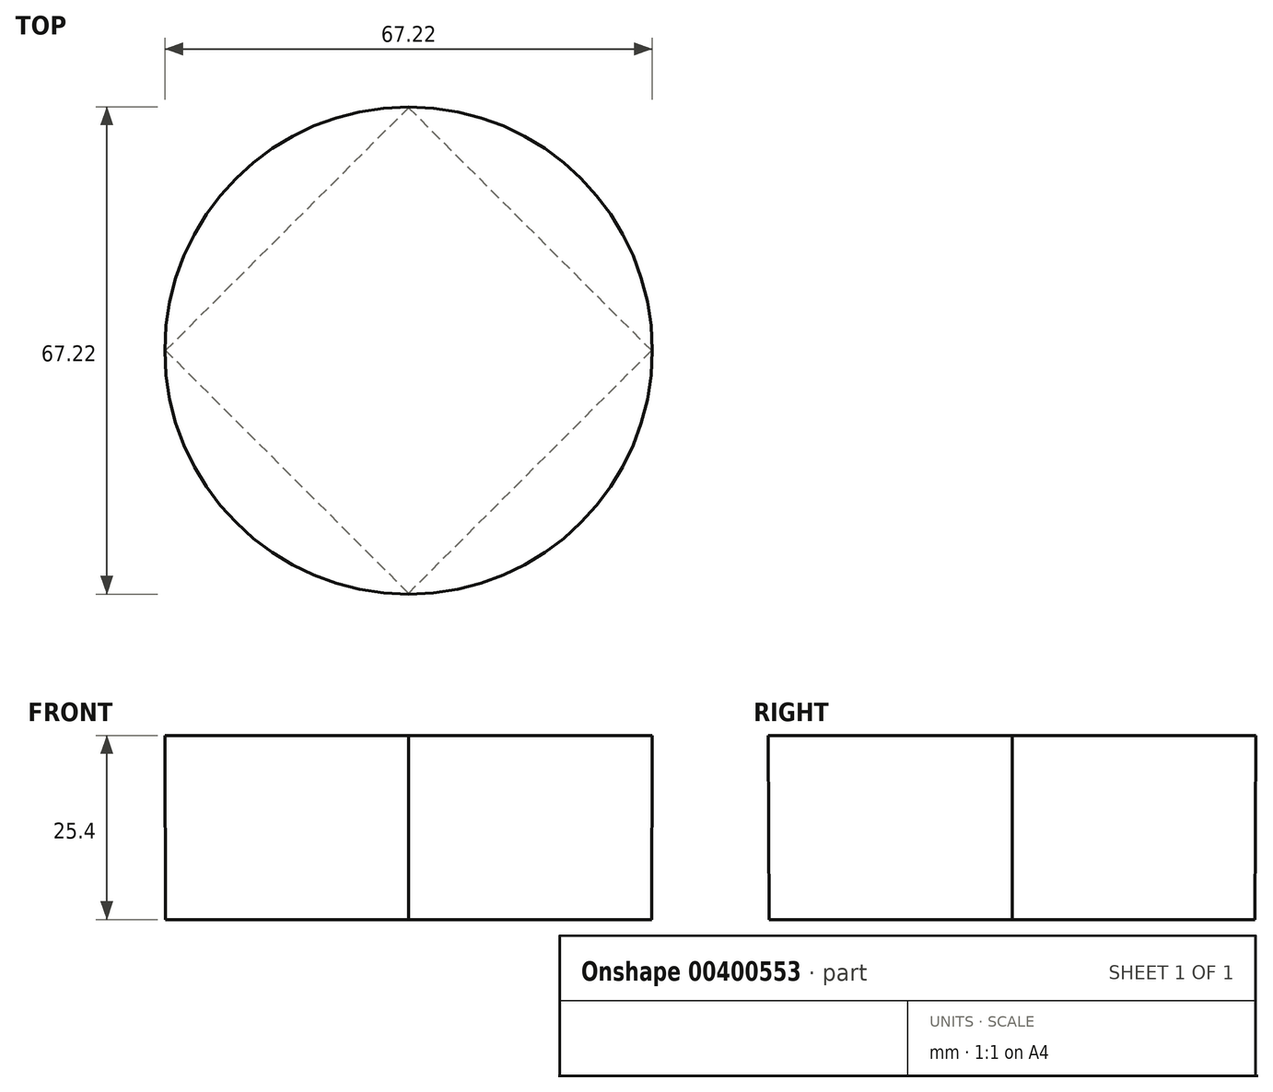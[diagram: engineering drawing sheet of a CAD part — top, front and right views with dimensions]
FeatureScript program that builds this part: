
annotation { "Feature Type Name" : "Feature", "Feature Type Description" : "" }
export const myFeature = defineFeature(function(context is Context, id is Id, definition is map)
    precondition{}
    {
        {
            var Q0;
            Q0=qCreatedBy(makeId("Top.planeOp"),FACE);
            cPlane(context, id + "F0", {"entities" : qUnion([Q0]), "cplaneType" : CPlaneType.OFFSET, "offset" : 25.4 * mm, "width" : 152.4 * mm, "height" : 152.4 * mm});
        }
        {
            var Q0;
            Q0=qCreatedBy(id+"F0.planeOp",FACE);
            var sketch = newSketch(context, id + "F1", { "sketchPlane" : qUnion([Q0])});
            skCircle(sketch, "E0", {"center": v(0, 0) * mm, "radius": 33.61 * mm});
            skSolve(sketch);
        }
        {
            var Q0;
            Q0=qCreatedBy(makeId("Top.planeOp"),FACE);
            var sketch = newSketch(context, id + "F2", { "sketchPlane" : qUnion([Q0])});
            skLineSegment(sketch, "E1", {"start": v(-33.5, 0) * mm, "end": v(0, 33.5) * mm});
            skLineSegment(sketch, "E2", {"start": v(0, 33.5) * mm, "end": v(33.5, 0) * mm});
            skLineSegment(sketch, "E3", {"start": v(33.5, 0) * mm, "end": v(0, -33.5) * mm});
            skLineSegment(sketch, "E4", {"start": v(0, -33.5) * mm, "end": v(-33.5, 0) * mm});
            skSolve(sketch);
        }
        {
            var Q0;
            Q0 = qSketchRegion(id + "F1", true);
            var Q1;
            Q1 = qSketchRegion(id + "F2", true);
            loft(context, id + "F3", {"sheetProfilesArray" : [{ "sheetProfileEntities" : qUnion([Q0]) }, { "sheetProfileEntities" : qUnion([Q1]) }]});
        }
    });
